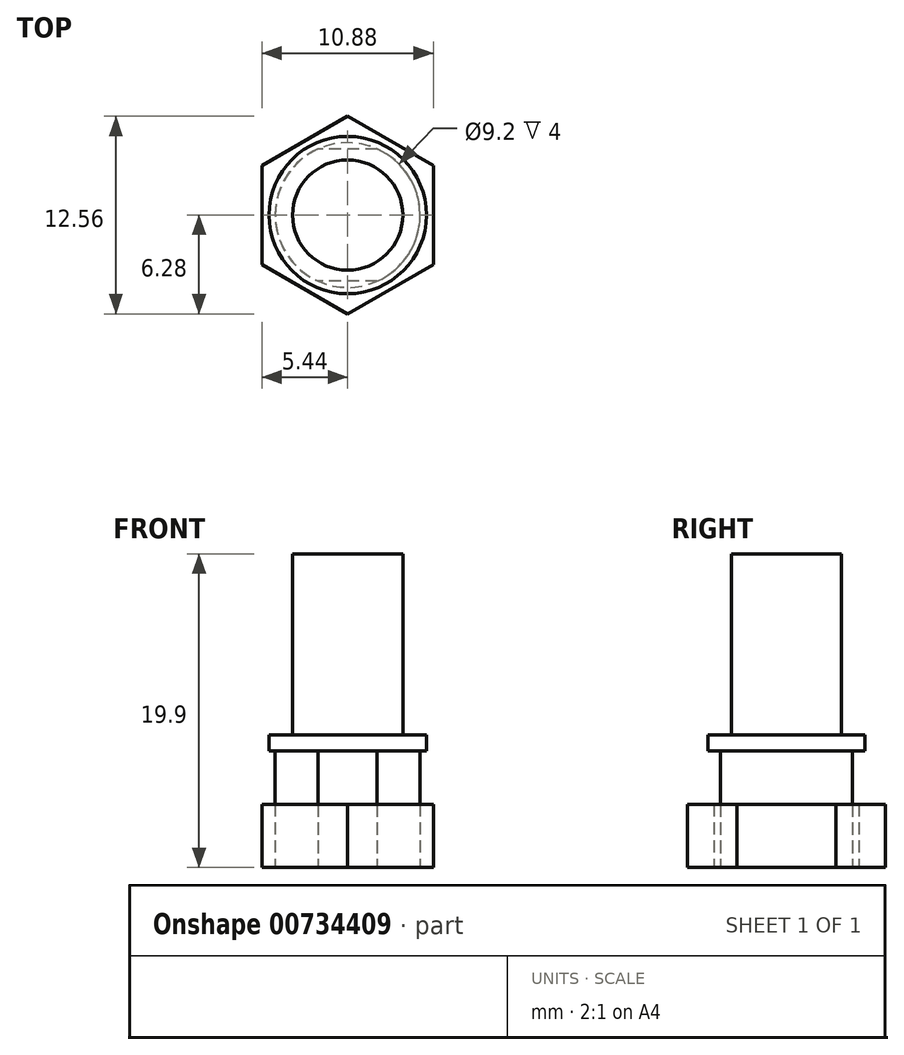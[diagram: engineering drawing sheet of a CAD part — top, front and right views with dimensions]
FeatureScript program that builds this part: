
annotation { "Feature Type Name" : "Feature", "Feature Type Description" : "" }
export const myFeature = defineFeature(function(context is Context, id is Id, definition is map)
    precondition{}
    {
        {
            var Q0;
            Q0=qCreatedBy(makeId("Top.planeOp"),FACE);
            var sketch = newSketch(context, id + "F0", { "sketchPlane" : qUnion([Q0])});
            skCircle(sketch, "E0", {"center": v(0, 0) * mm, "radius": 4.6 * mm});
            skLineSegment(sketch, "E1.bottom", {"start": v(5.96, 4.2) * mm, "end": v(-5.96, 4.2) * mm});
            skLineSegment(sketch, "E1.top", {"start": v(5.96, -4.2) * mm, "end": v(-5.96, -4.2) * mm});
            skLineSegment(sketch, "E1.left", {"start": v(5.96, 4.2) * mm, "end": v(5.96, -4.2) * mm});
            skLineSegment(sketch, "E1.right", {"start": v(-5.96, 4.2) * mm, "end": v(-5.96, -4.2) * mm});
            skSolve(sketch);
        }
        {
            var Q0;
            Q0=makeQuery(id+"F0.imprint","IMPRINT",FACE,{"disambiguationData":[TD([[makeQuery(id+"F0.imprint","IMPRINT",EDGE,{"derivedFrom":sQuery(id+"F0.wireOp",EDGE,"E0")}),1.0]])]});
            extrude(context, id + "F1", {"entities" : qUnion([Q0]), "depth" : (18.9 - 11.5) * mm, "offsetDistance" : 25 * mm});
        }
        {
            var Q0;
            Q0=makeQuery(id+"F1.opExtrude","CAP_FACE",FACE,{"disambiguationData":[OSD([sQuery(id+"F0.wireOp",EDGE,"E0")])],"isStart":false});
            var sketch = newSketch(context, id + "F2", { "sketchPlane" : qUnion([Q0])});
            skCircle(sketch, "E2", {"center": v(0, 0) * mm, "radius": 5 * mm});
            skSolve(sketch);
        }
        {
            var Q0;
            Q0=makeQuery(id+"F2.imprint","IMPRINT",FACE,{"disambiguationData":[TD([[makeQuery(id+"F2.imprint","IMPRINT",EDGE,{"derivedFrom":sQuery(id+"F2.wireOp",EDGE,"E2")}),1.0]])]});
            var Q1;
            Q1=makeQuery(id+"F2.imprint","IMPRINT",FACE,{"disambiguationData":[TD([[makeQuery(id+"F2.imprint","IMPRINT",EDGE,{"derivedFrom":makeQuery(id+"F1.opExtrude","CAP_EDGE",EDGE,{"disambiguationData":[OSD([sQuery(id+"F0.wireOp",EDGE,"E0")])],"isStart":false})}),1.0]])]});
            extrude(context, id + "F3", {"entities" : qUnion([Q0, Q1]), "operationType" : NewBodyOperationType.ADD, "depth" : 1 * mm, "offsetDistance" : 25 * mm});
        }
        {
            var Q0;
            Q0=makeQuery(id+"F3.opExtrude","CAP_FACE",FACE,{"disambiguationData":[OSD([sQuery(id+"F2.wireOp",EDGE,"E2")])],"isStart":false});
            var sketch = newSketch(context, id + "F4", { "sketchPlane" : qUnion([Q0])});
            skCircle(sketch, "E3", {"center": v(0, 0) * mm, "radius": 3.5 * mm});
            skSolve(sketch);
        }
        {
            var Q0;
            Q0=makeQuery(id+"F4.imprint","IMPRINT",FACE,{"disambiguationData":[TD([[makeQuery(id+"F4.imprint","IMPRINT",EDGE,{"derivedFrom":sQuery(id+"F4.wireOp",EDGE,"E3")}),1.0]])]});
            extrude(context, id + "F5", {"entities" : qUnion([Q0]), "operationType" : NewBodyOperationType.ADD, "depth" : 11.5 * mm, "offsetDistance" : 25 * mm});
        }
        {
            var Q0;
            Q0=makeQuery(id+"F0.imprint","IMPRINT",FACE,{"disambiguationData":[TD([[makeQuery(id+"F0.imprint","IMPRINT",EDGE,{"derivedFrom":sQuery(id+"F0.wireOp",EDGE,"E0")}),1.0]])]});
            var sketch = newSketch(context, id + "F6", { "sketchPlane" : qUnion([Q0])});
            skCircle(sketch, "E4.cCircle", {"center": v(0, 0) * mm, "radius": 5.44 * mm, "construction": true});
            skLineSegment(sketch, "E4.0", {"start": v(-5.44, -3.14) * mm, "end": v(-5.44, 3.14) * mm});
            skLineSegment(sketch, "E4.1", {"start": v(-5.44, 3.14) * mm, "end": v(0, 6.28) * mm});
            skLineSegment(sketch, "E4.2", {"start": v(0, 6.28) * mm, "end": v(5.44, 3.14) * mm});
            skLineSegment(sketch, "E4.3", {"start": v(5.44, 3.14) * mm, "end": v(5.44, -3.14) * mm});
            skLineSegment(sketch, "E4.4", {"start": v(5.44, -3.14) * mm, "end": v(0, -6.28) * mm});
            skLineSegment(sketch, "E4.5", {"start": v(0, -6.28) * mm, "end": v(-5.44, -3.14) * mm});
            skPoint(sketch, "E4.0.midPoint", {"position": v(-5.44, 0) * mm});
            skCircle(sketch, "E5.0", {"center": v(0, 0) * mm, "radius": 4.6 * mm});
            skSolve(sketch);
        }
        {
            var Q0;
            Q0=makeQuery(id+"F6.imprint","IMPRINT",FACE,{"disambiguationData":[TD([[makeQuery(id+"F6.imprint","IMPRINT",EDGE,{"derivedFrom":sQuery(id+"F6.wireOp",EDGE,"E4.0")}),-1.0]])]});
            extrude(context, id + "F7", {"entities" : qUnion([Q0]), "depth" : 4 * mm, "offsetDistance" : 25 * mm});
        }
    });
